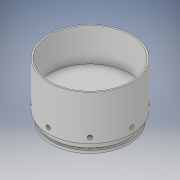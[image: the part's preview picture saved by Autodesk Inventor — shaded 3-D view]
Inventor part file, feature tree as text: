
AUTODESK INVENTOR PART (.ipt)
format: ipt  version: 2017 (Build 210142000, 142)  size: 164,864 bytes
history: native  units: in
note: dims shown in document units (in); Inventor stores cm internally (conversion verified against a paired STEP export)
features: sketch x3, extrude x2, revolve x1, pattern_circular x1
ambient origin geometry x8: Origin, YZ Plane, XZ Plane, XY Plane, X Axis, Y Axis, Z Axis, Center Point
bodies: Solid1 (feature_tree)
feature tree (7):
  revolve  "Revolution1"  [1 undecoded]
  extrude  "Extrusion1"  TaperAngle=90.0deg  [1 undecoded]
  extrude  "Extrusion2"  Depth=0.5in
  pattern_circular  "Circular Pattern1"  [2 undecoded]
  sketch  "Sketch1"  dims[d1=0.188in d2=3.5in]
  sketch  "Sketch2"  dims[d3=0.0in d4=90.0deg]
  sketch  "Sketch3"  dims[d5=3.75in d6=0.25in d7=0.5in d8=1.0in d9=7.5in d10=7.25in d11=3.0in d12=0.0in d13=0.25in d14=0.5in d15=0.375in d16=5.0in d17=0.0in d18=3.1496in d19=360.0deg d21=0.25in]
note: 4 required parameter values undecoded (feature->parameter linkage not recoverable at this tier; creation-order binding heuristic only, values carry confidence <= 0.55)